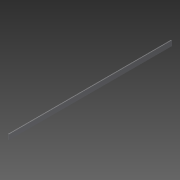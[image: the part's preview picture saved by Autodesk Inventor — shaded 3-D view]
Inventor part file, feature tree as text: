
AUTODESK INVENTOR PART (.ipt)
format: ipt  version: 2013 (Build 170138000, 138)  size: 64,512 bytes
history: native  units: in
note: dims shown in document units (in); Inventor stores cm internally (conversion verified against a paired STEP export)
features: extrude x1, sketch x1
ambient origin geometry x8: Origin, YZ Plane, XZ Plane, XY Plane, X Axis, Y Axis, Z Axis, Center Point
bodies: Solid1 (feature_tree)
feature tree (2):
  extrude  "Extrusion1"  Depth=48.0in
  sketch  "Sketch1"  dims[d0=1.5in d1=48.0in d2=0.25in d3=0.0in]
